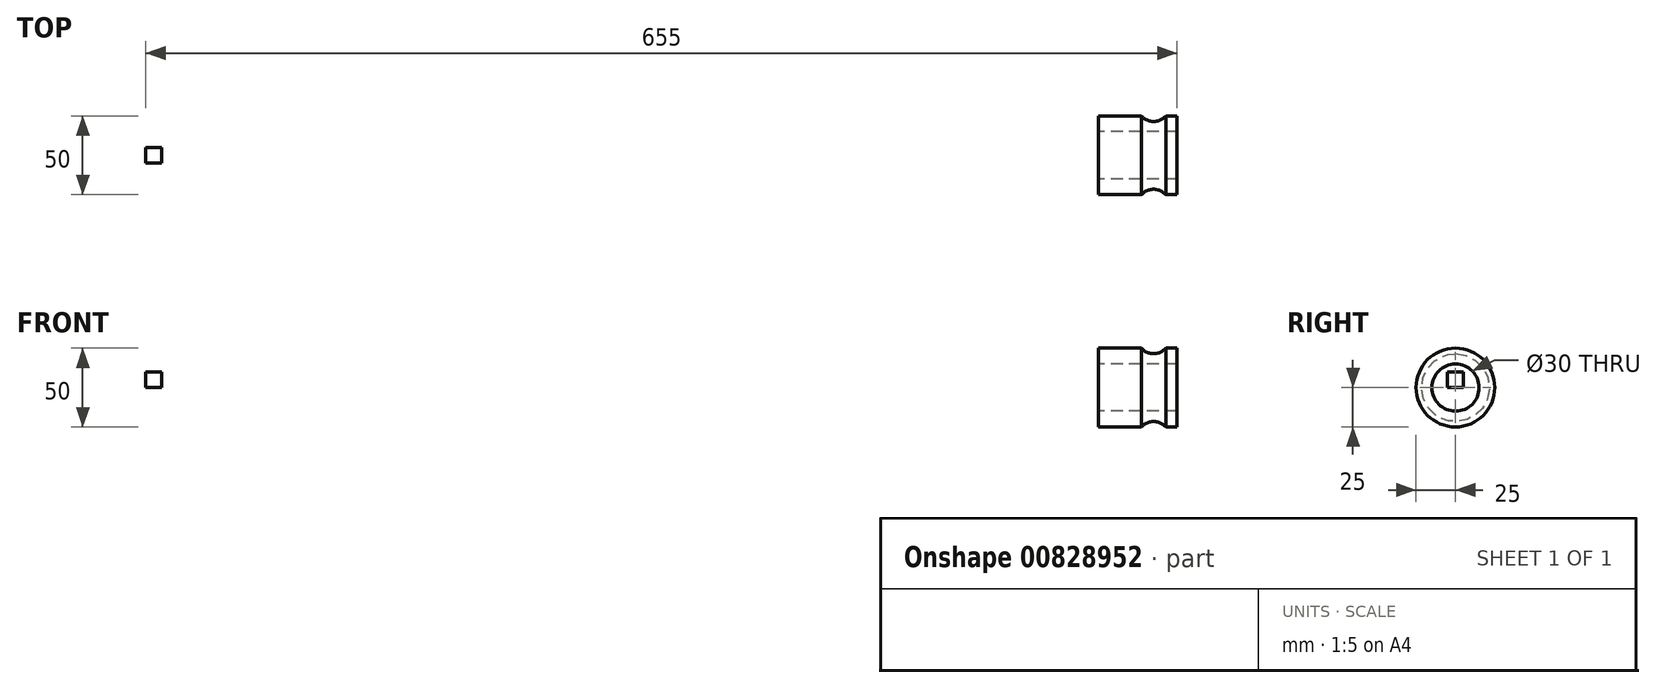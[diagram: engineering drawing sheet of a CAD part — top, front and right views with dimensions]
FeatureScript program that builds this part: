
annotation { "Feature Type Name" : "Feature", "Feature Type Description" : "" }
export const myFeature = defineFeature(function(context is Context, id is Id, definition is map)
    precondition{}
    {
        {
            var Q0;
            Q0=qCreatedBy(makeId("Top.planeOp"),FACE);
            var sketch = newSketch(context, id + "F0", { "sketchPlane" : qUnion([Q0])});
            skLineSegment(sketch, "E0.bottom", {"start": v(5, -5) * mm, "end": v(-5, -5) * mm});
            skLineSegment(sketch, "E0.top", {"start": v(5, 5) * mm, "end": v(-5, 5) * mm});
            skLineSegment(sketch, "E0.left", {"start": v(5, -5) * mm, "end": v(5, 5) * mm});
            skLineSegment(sketch, "E0.right", {"start": v(-5, -5) * mm, "end": v(-5, 5) * mm});
            skPoint(sketch, "E0.middle", {"position": v(0, 0) * mm});
            skLineSegment(sketch, "E1", {"start": v(0, 0) * mm, "end": v(600, 0) * mm});
            skLineSegment(sketch, "E2", {"start": v(600, 0) * mm, "end": v(650, 0) * mm});
            skLineSegment(sketch, "E3", {"start": v(650, 0) * mm, "end": v(650, 25) * mm});
            skLineSegment(sketch, "E4", {"start": v(650, 25) * mm, "end": v(642.86, 25) * mm});
            skLineSegment(sketch, "E5", {"start": v(600, 25) * mm, "end": v(600, 0) * mm});
            skLineSegment(sketch, "E6", {"start": v(650, 25) * mm, "end": v(650, 15) * mm});
            skLineSegment(sketch, "E7", {"start": v(650, 15) * mm, "end": v(600, 15) * mm});
            skArc(sketch, "E8", {"start": v(627.4, 25) * mm, "mid": v(635.13, 21.52) * mm, "end": v(642.86, 25) * mm});
            skLineSegment(sketch, "E9.trimOffspring", {"start": v(627.4, 25) * mm, "end": v(600, 25) * mm});
            skSolve(sketch);
        }
        {
            var Q0;
            Q0=makeQuery(id+"F0.imprint","IMPRINT",FACE,{"disambiguationData":[TD([[makeQuery(id+"F0.imprint","IMPRINT",EDGE,{"derivedFrom":sQuery(id+"F0.wireOp",EDGE,"E0.bottom")}),-1.0]])]});
            extrude(context, id + "F1", {"entities" : qUnion([Q0]), "depth" : 10 * mm, "offsetDistance" : 25 * mm});
        }
        {
            var Q0;
            {var subQ0=sQuery(id+"F0.wireOp",EDGE,"E4");Q0=makeQuery(id+"F0.imprint","IMPRINT",FACE,{"disambiguationData":[TD([[makeQuery(id+"F0.imprint","IMPRINT",EDGE,{"derivedFrom":subQ0}),1.0]])]});}
            var Q1;
            Q1=sQuery(id+"F0.wireOp",EDGE,"E2");
            revolve(context, id + "F2", {"surfaceOperationType" : NewSurfaceOperationType.NEW, "entities" : qUnion([Q0]), "axis" : qUnion([Q1]), "revolveType" : RevolveType.FULL});
        }
    });
